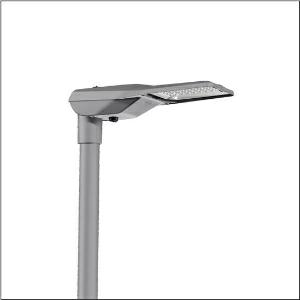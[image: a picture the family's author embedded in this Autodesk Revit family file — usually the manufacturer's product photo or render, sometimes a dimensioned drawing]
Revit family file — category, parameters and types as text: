
# Revit family: streetlight_sl_21_iq_mini___st1_5a_5xe2p31y08gb_2fd1
name_source: partatom
category: Lighting Fixtures
units: mm (PartAtom-declared; Revit-internal decimal feet)

## family parameters
Cut with Voids When Loaded = No
Host = Face
Light Source = No
Part Type = Normal
Room Calculation Point = No
Round Connector Dimension = Use Diameter
Shared = No

## types (1)
- --- (1 x LED, 5880 lm, 39.8 W, 3000K)
    Apparent Load = 40 VA
    CIE Flux Codes = 22 53 95 100 100
    Color Rendering = 70
    Color Temperature = 3000K
    Default Elevation = 1800 mm
    Description = Streetlight SL 21 iQ mini, mast luminaire, primary light control with lens, of PMMA, primary optical cover: cover, of toughened safety glass, transparent, light distribution: ST1.5a, light emission: direct distribution, primary light characteristic: asymmetric, installation type: post-top, side-entry, LED, High Power LED, rated luminous flux: 5.880lm, luminous efficacy: 148lm/W, light colour: 730, colour temperature: 3000K, control: presetting dimming logarithmic, Street-Remote, Auto-Match, Temp-Guard, Lumen-Switch, Night-Set, Smart-Wire, Light-Fading, Desk-Remote (wireless, voltage-free reading and setting of iQ features in the workshop via application-optimized NFC function/RFID function), optimised constant luminous flux control (CLO 2.0), mains connection: 220..240V, AC, 50/60Hz, start of lifetime: 40W, end of service life: 41W, reduction: 18W, luminaire housing, of diecast aluminium, powder-coated, Siteco® metallic grey (DB 702S), corrosivity category C5 mid according to DIN EN ISO 12944, please order mast flange separately, inclination adjustable: 0°, 5°, 10°, 15°, sealing non-destructively replaceable, multi-level sealing system, length: 628mm, width: 235mm, height: 110mm, mast flange for spigot size: 42mm (side-entry): 5XC10008XM4, 60/48mm (side-entry/post-top): 5XC10108XM2, 76/60mm (side-entry/post-top): 5XC10108XM1, Smart Interface below and above, protection rating (complete): IP66, insulation class (complete): insulation class II (safety insulation), certification: CE, ENEC, ENEC+, VDE, impact resistance: IK09, permissible operating ambient temperature for outdoor applications: -40..+50°C, standard-compliant lighting for roads and squares, packaging unit: 1 piece

Light Distribution: ST1.5a
    Height = 110 mm
    Lamp = 1 x LED
    Lamp Light Flux = 5880 lm
    Lamp Power = 39.8 W
    Lamp count = 1
    Length = 625 mm
    Luminous efficacy = 148 lm/W
    Manufacturer = Siteco
    ModVariant = No
    Model = 5XE2P31Y08GB
    Number of Poles = 1
    OnlyDefault = Yes
    Power Factor = 1
    Product Name = Streetlight SL 21 iQ mini | ST1.5a
    Product group = mast luminaire | pylon top
    ProductGroupID = 6100
    Protection Class = Protection class II
    Protection Degree = IP 66
    RLX_Detail_Level = 1
    RLX_Emergency_Light_Flux = 0 lm
    RLX_Emergency_Type = 0
    RLX_Emergency_Type_DB = No
    RlxData = <blob elided: 96269 chars, md5=a777ffc0>
    Socket = socket
    Standby Power = 0 W
    System Light Flux = 5880 lm
    System Power = 40 W
    Type Comments = factory setting: luminous flux: 100 % | dim-lin: 254 | 800 mA
    Type Image = l_1003514.jpg
    URL = http://relux.com
    VarID = @adj_042025
    Voltage = 0 V
    Weight = 0.00 kg
    Width = 234 mm

## geometry (parser evidence)
native form markers: Blend x4, Sweep x10
no freeform markers — native parametric forms only
